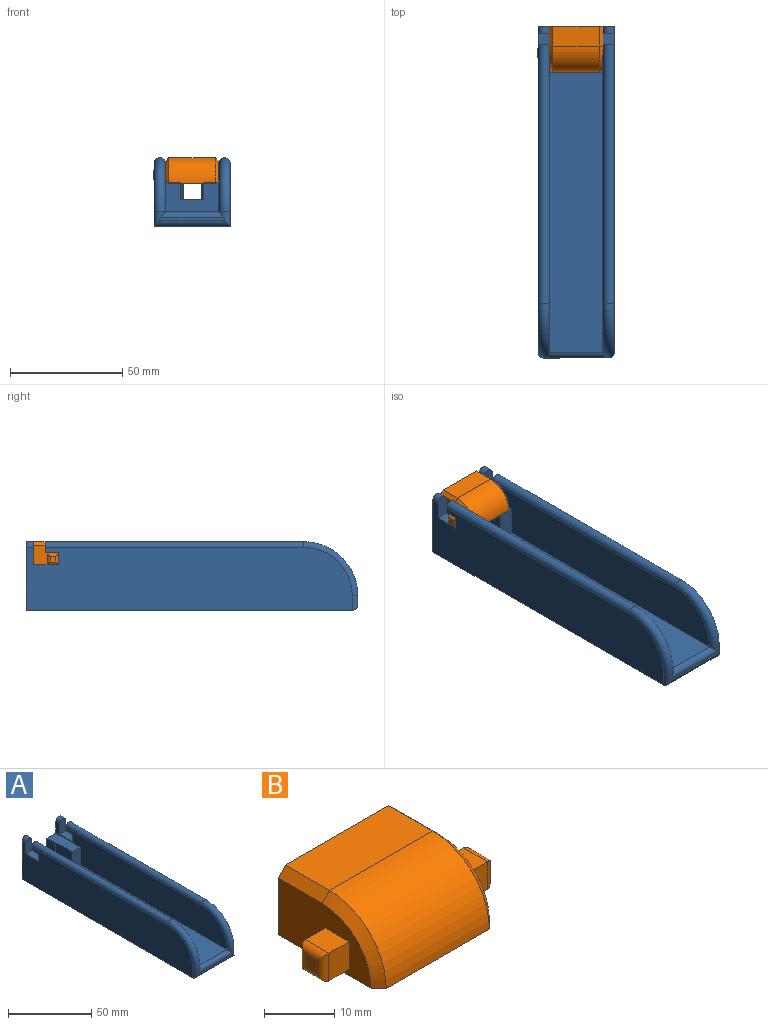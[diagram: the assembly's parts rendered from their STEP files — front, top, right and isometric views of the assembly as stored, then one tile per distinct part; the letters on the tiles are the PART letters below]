
ASSEMBLY  parts=2 mates=1
PART A: 36 faces, bbox 33.9x149.6x32.5 mm
  f0: plane 145.03x27.94mm, normal (1,0,0), area 3880.5mm2, adj f5,f8,f16,f17,f18,f19,f20,f26
  f1: plane 145.03x27.94mm, normal (-1,0,0), area 3880.5mm2, adj f5,f8,f21,f22,f23,f24,f25,f31
  f2: plane 145.03x21.59mm, normal (1,0,0), area 2694.1mm2, adj f4,f5,f6,f9,f21,f22,f23,f24
  f3: plane 145.03x21.59mm, normal (-1,0,0), area 2694.1mm2, adj f5,f6,f9,f10,f16,f17,f18,f19
  f4: plane 20.57x7.81mm, normal (0,0,1), area 142mm2, adj f2,f5,f9,f11,f12
  f5: plane 33.91x30.48mm, normal (0,1,0), area 700.1mm2, adj f0,f1,f2,f3,f4,f8,f10,f11
  f6: plane 124.46x23.75mm, normal (0,0,1), area 2955.8mm2, adj f2,f3,f9,f30
  f7: plane 28.83x1.27mm, normal (0,-1,0), area 36.6mm2, adj f28,f29,f30,f31
  f8: plane 145.03x33.91mm, normal (0,0,-1), area 4918mm2, adj f0,f1,f5,f29
  f9: plane 23.75x12.9mm, normal (0,-1,0), area 228.8mm2, adj f2,f3,f4,f6,f10,f12,f13,f15
  f10: plane 20.57x7.81mm, normal (0,0,1), area 142mm2, adj f3,f5,f9,f13,f14
  f11: plane 7.54x6.6mm, normal (0.99,-0.16,0), area 50.5mm2, adj f4,f5,f12,f15
  f12: plane 13.97x7.54mm, normal (1,0,0), area 105.4mm2, adj f4,f9,f11,f15
  f13: plane 13.97x7.54mm, normal (-1,0,0), area 105.4mm2, adj f9,f10,f14,f15
  f14: plane 7.54x6.6mm, normal (-0.99,-0.16,0), area 50.5mm2, adj f5,f10,f13,f15
  f15: plane 20.57x10.29mm, normal (0,0,1), area 204.5mm2, adj f5,f9,f11,f12,f13,f14
  f16: plane 5.08x4.83mm, normal (0,1,0), area 21.8mm2, adj f0,f3,f20,f26
  f17: plane 5.46x5.08mm, normal (0,1,0), area 27.7mm2, adj f0,f3,f18,f20
  f18: plane 10.99x5.08mm, normal (0,0,1), area 55.8mm2, adj f0,f3,f17,f19
  f19: plane 10.29x5.08mm, normal (0,-1,0), area 49.5mm2, adj f0,f3,f18,f34
  f20: plane 5.91x5.08mm, normal (0,0,-1), area 30mm2, adj f0,f3,f16,f17
  f21: plane 5.91x5.08mm, normal (0,0,-1), area 30mm2, adj f1,f2,f22,f25
  f22: plane 5.08x4.83mm, normal (0,1,0), area 21.8mm2, adj f1,f2,f21,f33
  f23: plane 10.29x5.08mm, normal (0,-1,0), area 49.5mm2, adj f1,f2,f24,f35
  f24: plane 10.99x5.08mm, normal (0,0,1), area 55.8mm2, adj f1,f2,f23,f25
  f25: plane 5.46x5.08mm, normal (0,1,0), area 27.7mm2, adj f1,f2,f21,f24
  f26: cylinder r=2.54mm len=115mm, axis (0,1,0), area 917.6mm2, adj f0,f3,f16,f27
  f27: torus R=21.59mm, axis (1,0,0), area 290.9mm2, adj f0,f3,f26,f28
  f28: cylinder r=2.54mm len=6.35mm, axis (0,0,-1), area 25.3mm2, adj f0,f7,f27,f29,f30
  f29: cylinder r=2.54mm len=33.91mm, axis (-1,0,0), area 127.9mm2, adj f7,f8,f28,f31
  f30: cylinder r=2.54mm len=28.83mm, axis (1,0,0), area 102.1mm2, adj f6,f7,f28,f31
  f31: cylinder r=2.54mm len=6.35mm, axis (0,0,1), area 25.3mm2, adj f1,f7,f29,f30,f32
  f32: torus R=21.59mm, axis (1,0,0), area 290.9mm2, adj f1,f2,f31,f33
  f33: cylinder r=2.54mm len=115mm, axis (0,-1,0), area 917.6mm2, adj f1,f2,f22,f32
  f34: cylinder r=2.54mm len=5.08mm, axis (0,1,0), area 26.9mm2, adj f0,f3,f5,f19
  f35: cylinder r=2.54mm len=5.08mm, axis (0,-1,0), area 26.9mm2, adj f1,f2,f5,f23
PART B: 28 faces, bbox 34.5x20.3x11.4 mm
  f0: plane 18.8x9.91mm, normal (1,0,0), area 141.8mm2, adj f2,f4,f10,f11,f12,f13,f18,f19
  f1: plane 18.8x9.91mm, normal (-1,0,0), area 141.8mm2, adj f2,f4,f5,f6,f7,f8,f16,f17
  f2: plane 23.88x11.43mm, normal (0,1,0), area 270.6mm2, adj f0,f1,f3,f4,f16,f19
  f3: plane 20.83x8.89mm, normal (0,0,1), area 185.2mm2, adj f2,f15,f16,f19
  f4: plane 23.88x20.32mm, normal (0,0,-1), area 482.8mm2, adj f0,f1,f2,f15,f17,f18
  f5: plane 4.83x4.06mm, normal (0,0,-1), area 19.6mm2, adj f1,f6,f8,f24
  f6: plane 4.83x4.06mm, normal (0,-1,0), area 19.6mm2, adj f1,f5,f7,f25
  f7: plane 4.83x4.06mm, normal (0,0,1), area 19.6mm2, adj f1,f6,f8,f27
  f8: plane 4.83x4.06mm, normal (0,1,0), area 19.6mm2, adj f1,f5,f7,f26
  f9: plane 2.29x2.29mm, normal (-1,0,0), area 5.2mm2, adj f24,f25,f26,f27
  f10: plane 4.83x4.06mm, normal (0,0,-1), area 19.6mm2, adj f0,f11,f13,f20
  f11: plane 4.83x4.06mm, normal (0,1,0), area 19.6mm2, adj f0,f10,f12,f22
  f12: plane 4.83x4.06mm, normal (0,0,1), area 19.6mm2, adj f0,f11,f13,f23
  f13: plane 4.83x4.06mm, normal (0,-1,0), area 19.6mm2, adj f0,f10,f12,f21
  f14: plane 2.29x2.29mm, normal (1,0,0), area 5.2mm2, adj f20,f21,f22,f23
  f15: cylinder r=11.43mm len=20.83mm, axis (-1,0,0), area 374mm2, adj f3,f4,f17,f18
  f16: plane 8.89x1.52mm, normal (-0.71,0,0.71), area 19.2mm2, adj f1,f2,f3,f17
  f17: cone r=9.91mm half-angle=45deg, axis (1,0,0), area 36.1mm2, adj f1,f4,f15,f16
  f18: cone r=9.91mm half-angle=45deg, axis (-1,0,0), area 36.1mm2, adj f0,f4,f15,f19
  f19: plane 8.89x1.52mm, normal (0.71,0,0.71), area 19.2mm2, adj f0,f2,f3,f18
  f20: cylinder r=1.27mm len=4.83mm, axis (0,-1,0), area 7.8mm2, adj f10,f14,f21,f22
  f21: cylinder r=1.27mm len=4.83mm, axis (0,0,1), area 7.8mm2, adj f13,f14,f20,f23
  f22: cylinder r=1.27mm len=4.83mm, axis (0,0,-1), area 7.8mm2, adj f11,f14,f20,f23
  f23: cylinder r=1.27mm len=4.83mm, axis (0,1,0), area 7.8mm2, adj f12,f14,f21,f22
  f24: cylinder r=1.27mm len=4.83mm, axis (0,1,0), area 7.8mm2, adj f5,f9,f25,f26
  f25: cylinder r=1.27mm len=4.83mm, axis (0,0,-1), area 7.8mm2, adj f6,f9,f24,f27
  f26: cylinder r=1.27mm len=4.83mm, axis (0,0,1), area 7.8mm2, adj f8,f9,f24,f27
  f27: cylinder r=1.27mm len=4.83mm, axis (0,-1,0), area 7.8mm2, adj f7,f9,f25,f26
PLACE A rot(axis=(0.4,-0.4,0.83),0deg) t=(-98.05,46.01,7.58)mm
PLACE B rot(axis=(0.51,0.01,0.86),0deg) t=(-98.02,121.65,20.28)mm
MATE fastened B.f10 <-> A.f18  axis (0,0,1) through (-86.09,117.46,21.42)mm
